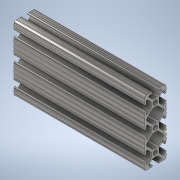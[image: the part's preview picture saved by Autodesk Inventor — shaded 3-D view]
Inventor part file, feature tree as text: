
AUTODESK INVENTOR PART (.ipt)
format: ipt  version: 2020 (Build 240168000, 168)  size: 376,320 bytes
history: native  units: in
note: dims shown in document units (in); Inventor stores cm internally (conversion verified against a paired STEP export)
features: sketch x2, extrude x1
ambient origin geometry x8: Origin, YZ Plane, XZ Plane, XY Plane, X Axis, Y Axis, Z Axis, Center Point
bodies: Solid1 (feature_tree)
feature tree (3):
  extrude  "Extrusion1"  [1 undecoded]
  sketch  "Sketch2"
  sketch  "Sketch1"  dims[d0=6.0in d1=0.0in]
note: 1 required parameter value undecoded (feature->parameter linkage not recoverable at this tier; creation-order binding heuristic only, values carry confidence <= 0.55)
